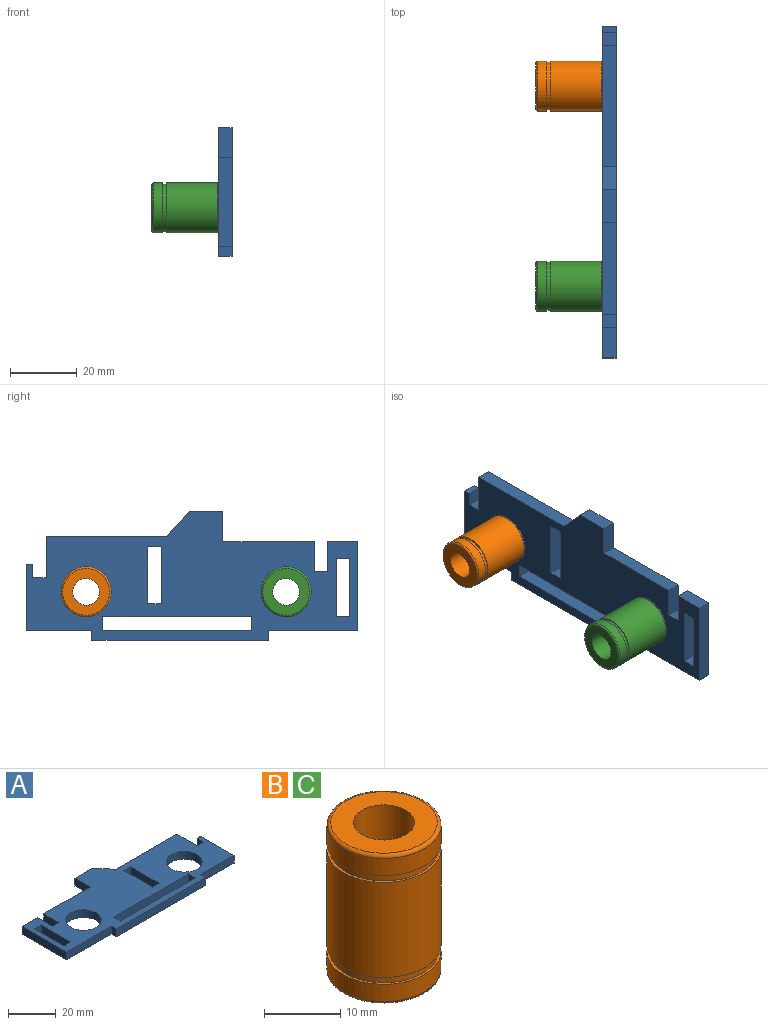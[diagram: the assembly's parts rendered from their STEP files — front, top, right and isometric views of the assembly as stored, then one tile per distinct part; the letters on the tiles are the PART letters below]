
ASSEMBLY  parts=3 mates=2
PART A: 36 faces, bbox 99.5x38.5x4 mm
  f0: plane 17x4mm, normal (1,0,0), area 68mm2, adj f1,f29,f34,f35
  f1: plane 4x4mm, normal (0,-1,0), area 16mm2, adj f0,f2,f34,f35
  f2: plane 17x4mm, normal (-1,0,0), area 68mm2, adj f1,f29,f34,f35
  f3: plane 17.5x4mm, normal (-1,0,0), area 70mm2, adj f4,f30,f34,f35
  f4: plane 4x4mm, normal (0,1,0), area 16mm2, adj f3,f5,f34,f35
  f5: plane 17.5x4mm, normal (1,0,0), area 70mm2, adj f4,f30,f34,f35
  f6: plane 44.5x4mm, normal (0,1,0), area 178mm2, adj f7,f31,f34,f35
  f7: plane 4x4mm, normal (1,0,0), area 16mm2, adj f6,f8,f34,f35
  f8: plane 44.5x4mm, normal (0,-1,0), area 178mm2, adj f7,f31,f34,f35
  f9: plane 26.75x4mm, normal (0,-1,0), area 107mm2, adj f10,f32,f34,f35
  f10: plane 4x3mm, normal (-1,0,0), area 12mm2, adj f9,f11,f34,f35
  f11: plane 53x4mm, normal (0,-1,0), area 212mm2, adj f10,f12,f34,f35
  f12: plane 4x3mm, normal (1,0,0), area 12mm2, adj f11,f13,f34,f35
  f13: plane 19.75x4mm, normal (0,-1,0), area 79mm2, adj f12,f14,f34,f35
  f14: plane 19.8x4mm, normal (1,0,0), area 79.2mm2, adj f13,f15,f34,f35
  f15: plane 4x2mm, normal (0,1,0), area 8mm2, adj f14,f16,f34,f35
  f16: plane 4x4mm, normal (-1,0,0), area 16mm2, adj f15,f17,f34,f35
  f17: plane 4x4mm, normal (0,1,0), area 16mm2, adj f16,f18,f34,f35
  f18: plane 12.14x4mm, normal (1,0,0), area 48.6mm2, adj f17,f19,f34,f35
  f19: plane 36.05x4mm, normal (0,1,0), area 144.2mm2, adj f18,f20,f34,f35
  f20: plane 7.56x6.95mm, normal (0.74,0.68,0), area 41.1mm2, adj f19,f21,f34,f35
  f21: plane 10x4mm, normal (0,1,0), area 40mm2, adj f20,f22,f34,f35
  f22: plane 9x4mm, normal (-1,0,0), area 36mm2, adj f21,f23,f34,f35
  f23: plane 27.5x4mm, normal (0,1,0), area 110mm2, adj f22,f24,f34,f35
  f24: plane 9x4mm, normal (-1,0,0), area 36mm2, adj f23,f25,f34,f35
  f25: plane 4x4mm, normal (0,1,0), area 16mm2, adj f24,f26,f34,f35
  f26: plane 9x4mm, normal (1,0,0), area 36mm2, adj f25,f27,f34,f35
  f27: plane 9x4mm, normal (0,1,0), area 36mm2, adj f26,f32,f34,f35
  f28: cylinder r=7.5mm len=15mm, axis (0,0,-1), area 188.5mm2, adj f34,f35
  f29: plane 4x4mm, normal (0,1,0), area 16mm2, adj f0,f2,f34,f35
  f30: plane 4x4mm, normal (0,-1,0), area 16mm2, adj f3,f5,f34,f35
  f31: plane 4x4mm, normal (-1,0,0), area 16mm2, adj f6,f8,f34,f35
  f32: plane 26.5x4mm, normal (-1,0,0), area 106mm2, adj f9,f27,f34,f35
  f33: cylinder r=7.5mm len=15mm, axis (0,0,-1), area 188.5mm2, adj f34,f35
  f34: plane 99.5x38.5mm, normal (0,0,1), area 2212.5mm2, adj f0,f1,f2,f3,f4,f5,f6,f7
  f35: plane 99.5x38.5mm, normal (0,0,-1), area 2212.5mm2, adj f0,f1,f2,f3,f4,f5,f6,f7
PART B: 14 faces, bbox 16.2x16.2x24 mm
  f0: plane 15x15mm, normal (0,0,-1), area 16.1mm2, adj f1,f10
  f1: cylinder r=7.15mm len=14.3mm, axis (0,0,-1), area 49.4mm2, adj f0,f2
  f2: plane 15x15mm, normal (0,0,1), area 16.1mm2, adj f1,f3
  f3: cylinder r=7.5mm len=15mm, axis (0,0,-1), area 129.6mm2, adj f2,f12
  f4: plane 14x14mm, normal (0,0,-1), area 103.7mm2, adj f11,f12
  f5: plane 14x14mm, normal (0,0,1), area 103.7mm2, adj f11,f13
  f6: cylinder r=7.5mm len=15mm, axis (0,0,-1), area 129.6mm2, adj f7,f13
  f7: plane 15x15mm, normal (0,0,-1), area 16.1mm2, adj f6,f8
  f8: cylinder r=7.15mm len=14.3mm, axis (0,0,-1), area 49.4mm2, adj f7,f9
  f9: plane 15x15mm, normal (0,0,1), area 16.1mm2, adj f8,f10
  f10: cylinder r=7.5mm len=15.3mm, axis (0,0,-1), area 721mm2, adj f0,f9
  f11: cylinder r=4mm len=24mm, axis (0,0,1), area 603.2mm2, adj f4,f5
  f12: torus R=7mm, axis (0,0,1), area 36.1mm2, adj f3,f4
  f13: torus R=7mm, axis (0,0,-1), area 36.1mm2, adj f5,f6
PART C: same geometry as B
PLACE A rot(axis=(0.58,0.58,0.58),120deg) t=(27.95,-78.95,27.88)mm
PLACE B rot(axis=(-0.58,-0.58,0.58),120deg) t=(31.95,2.55,12.88)mm
PLACE C rot(axis=(-0.58,-0.58,0.58),120deg) t=(31.95,-57.45,12.88)mm
MATE fastened B.f1 <-> A.f28  axis (1,0,0) through (31.95,2.55,12.88)mm
MATE fastened C.f1 <-> A.f33  axis (1,0,0) through (31.95,-57.45,12.88)mm
